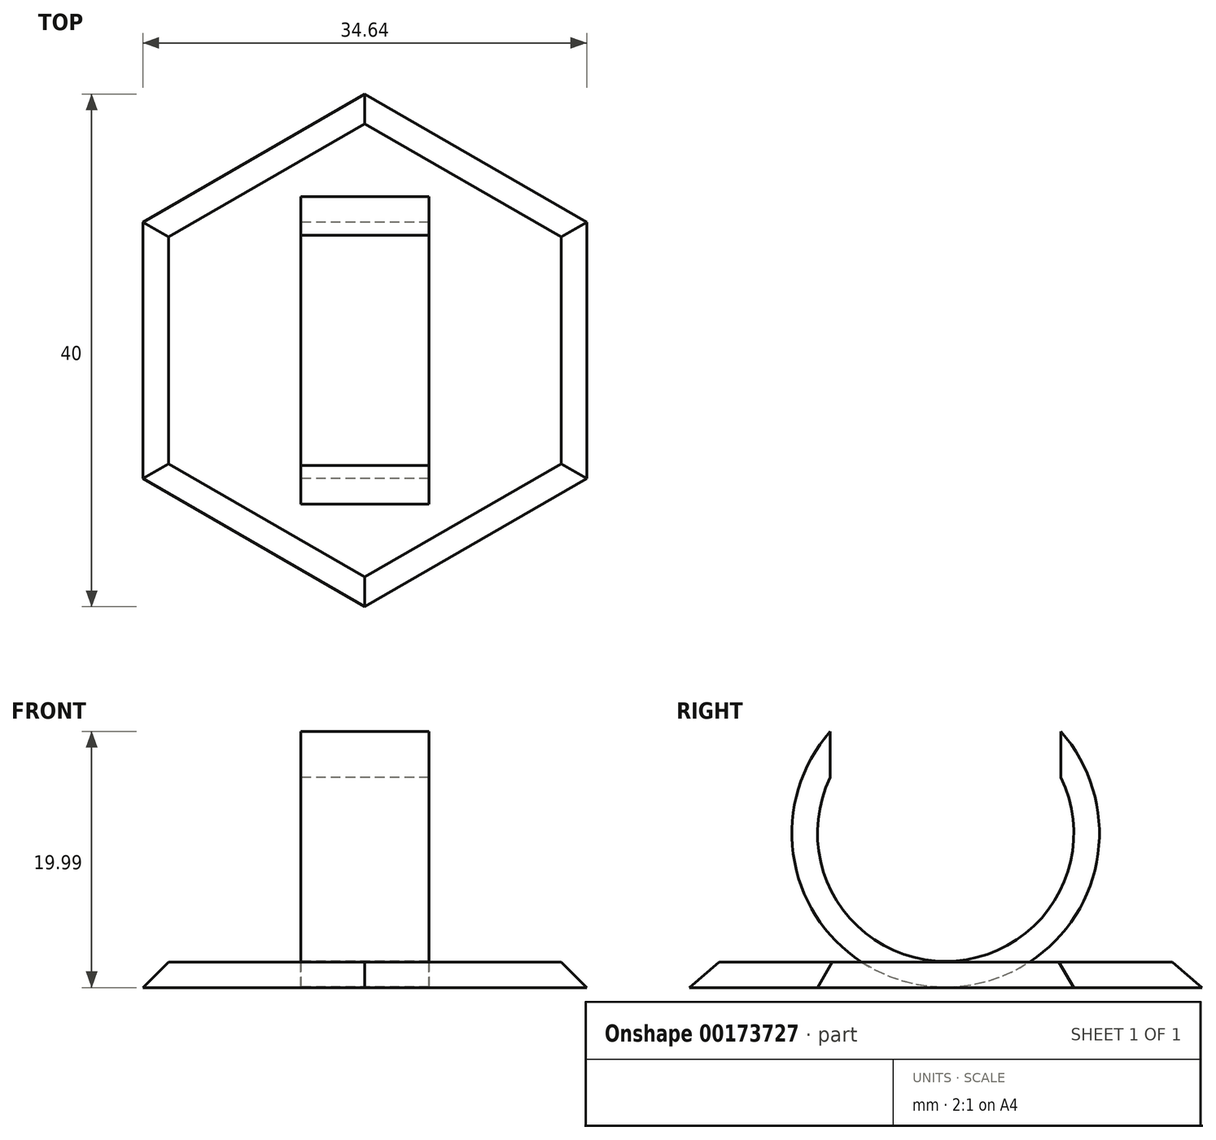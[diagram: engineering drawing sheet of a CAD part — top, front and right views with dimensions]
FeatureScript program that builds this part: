
annotation { "Feature Type Name" : "Feature", "Feature Type Description" : "" }
export const myFeature = defineFeature(function(context is Context, id is Id, definition is map)
    precondition{}
    {
        {
            var Q0;
            Q0=qCreatedBy(makeId("Top.planeOp"),FACE);
            var sketch = newSketch(context, id + "F0", { "sketchPlane" : qUnion([Q0])});
            skCircle(sketch, "E0.cCircle", {"center": v(0, 0) * mm, "radius": 20 * mm, "construction": true});
            skLineSegment(sketch, "E0.0", {"start": v(0, -20) * mm, "end": v(-17.32, -10) * mm});
            skLineSegment(sketch, "E0.1", {"start": v(-17.32, -10) * mm, "end": v(-17.32, 10) * mm});
            skLineSegment(sketch, "E0.2", {"start": v(-17.32, 10) * mm, "end": v(0, 20) * mm});
            skLineSegment(sketch, "E0.3", {"start": v(0, 20) * mm, "end": v(17.32, 10) * mm});
            skLineSegment(sketch, "E0.4", {"start": v(17.32, 10) * mm, "end": v(17.32, -10) * mm});
            skLineSegment(sketch, "E0.5", {"start": v(17.32, -10) * mm, "end": v(0, -20) * mm});
            skSolve(sketch);
        }
        {
            var Q0;
            Q0=makeQuery(id+"F0.imprint","IMPRINT",FACE,{"disambiguationData":[TD([[makeQuery(id+"F0.imprint","IMPRINT",EDGE,{"derivedFrom":sQuery(id+"F0.wireOp",EDGE,"E0.0")}),-1.0]])]});
            extrude(context, id + "F1", {"entities" : qUnion([Q0]), "depth" : 2 * mm, "hasDraft" : true, "draftAngle" : 45 * degree, "draftPullDirection" : true});
        }
        {
            var Q0;
            Q0=qCreatedBy(makeId("Right.planeOp"),FACE);
            var sketch = newSketch(context, id + "F2", { "sketchPlane" : qUnion([Q0])});
            skCircle(sketch, "E1", {"center": v(0, 12.05) * mm, "radius": 12 * mm});
            skCircle(sketch, "E2", {"center": v(0, 12.05) * mm, "radius": 10 * mm});
            skSolve(sketch);
        }
        {
            var Q0;
            Q0 = qSketchRegion(id + "F2", true);
            extrude(context, id + "F3", {"entities" : qUnion([Q0]), "depth" : 10 * mm, "symmetric" : true});
        }
        {
            var Q0;
            Q0=qCreatedBy(makeId("Right.planeOp"),FACE);
            var sketch = newSketch(context, id + "F4", { "sketchPlane" : qUnion([Q0])});
            skLineSegment(sketch, "E3.bottom", {"start": v(-9, 13.6) * mm, "end": v(9, 13.6) * mm});
            skLineSegment(sketch, "E3.top", {"start": v(-9, 31.6) * mm, "end": v(9, 31.6) * mm});
            skLineSegment(sketch, "E3.left", {"start": v(-9, 13.6) * mm, "end": v(-9, 31.6) * mm});
            skLineSegment(sketch, "E3.right", {"start": v(9, 13.6) * mm, "end": v(9, 31.6) * mm});
            skPoint(sketch, "E3.middle", {"position": v(0, 22.6) * mm});
            skSolve(sketch);
        }
        {
            var Q0;
            Q0=makeQuery(id+"F4.imprint","IMPRINT",FACE,{"disambiguationData":[TD([[makeQuery(id+"F4.imprint","IMPRINT",EDGE,{"derivedFrom":sQuery(id+"F4.wireOp",EDGE,"E3.bottom")}),1.0]])]});
            extrude(context, id + "F5", {"entities" : qUnion([Q0]), "operationType" : NewBodyOperationType.REMOVE, "oppositeDirection" : true, "depth" : 25 * mm, "symmetric" : true});
        }
    });
